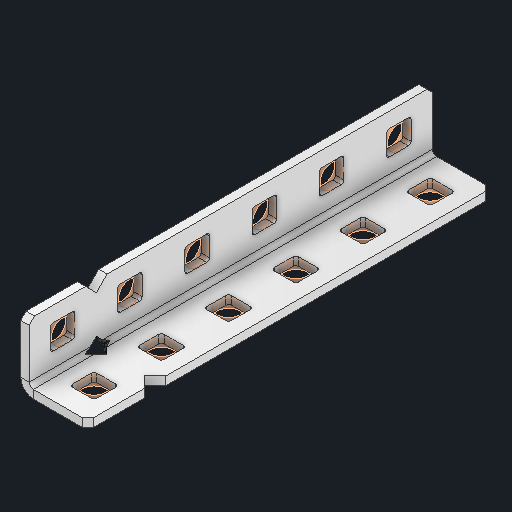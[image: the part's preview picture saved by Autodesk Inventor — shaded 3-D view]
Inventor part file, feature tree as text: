
AUTODESK INVENTOR PART (.ipt)
format: ipt  version: 2025 (Build 290162000, 162)  size: 401,920 bytes
history: native  units: in
note: dims shown in document units (in); Inventor stores cm internally (conversion verified against a paired STEP export)
features: other x33, sketch x2, sheet_metal_op x1
ambient origin geometry x8: Origin, YZ Plane, XZ Plane, XY Plane, X Axis, Y Axis, Z Axis, Center Point
bodies: Solid1 (feature_tree)
feature tree (36):
  other  "Alu Angle 1x1x6.ipt"
  other  "Solid1::Alu Angle 1x1x6.ipt"
  other  "TaggingFeature1"
  sketch  "Sketch1"  dims[d0=0.3937in]
  sketch  "Sketch2"  dims[d1=0.0625in]
  sheet_metal_op  "Body Pattern Sketch"
  other  "Arc Length"
  other  "Diagonal Plane"
  other  "Srf1"
  other  "Srf2"
  other  "Srf3"
  other  "Srf4"
  other  "Srf5"
  other  "Srf6"
  other  "Srf7"
  other  "Srf8"
  other  "Srf9"
  other  "Srf10"
  other  "Srf11"
  other  "Srf12"
  other  "Srf13"
  other  "Srf14"
  other  "Srf91::Derived"
  other  "Srf92::Derived"
  other  "Srf856::Derived"
  other  "Srf857::Derived"
  other  "Srf858::Derived"
  other  "Srf859::Derived"
  other  "Srf860::Derived"
  other  "Srf1275::Derived"
  other  "Srf1276::Derived"
  other  "Srf1278::Derived"
  other  "Srf1279::Derived"
  other  "Srf1280::Derived"
  other  "Srf1281::Derived"
  other  "Srf1282::Derived"
